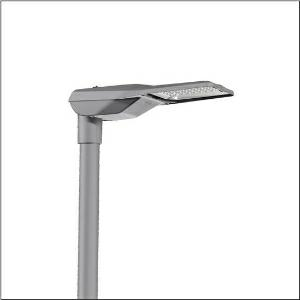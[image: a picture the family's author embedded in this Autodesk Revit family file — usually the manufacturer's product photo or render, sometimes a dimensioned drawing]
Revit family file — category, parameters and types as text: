
# Revit family: streetlight_sl_21_iq_mini___st1_0a_5xe2d31v08jb_ee78
name_source: partatom
category: Lighting Fixtures
units: mm (PartAtom-declared; Revit-internal decimal feet)

## family parameters
Cut with Voids When Loaded = No
Host = Face
Light Source = No
Part Type = Normal
Room Calculation Point = No
Round Connector Dimension = Use Diameter
Shared = No

## types (1)
- --- (1 x LED, 11210 lm, 72.5 W, 3000K)
    Apparent Load = 73 VA
    CIE Flux Codes = 40 73 97 100 100
    Color Rendering = 70
    Color Temperature = 3000K
    Default Elevation = 1800 mm
    Description = Streetlight SL 21 iQ mini, mast luminaire, primary light control with lens, of PMMA, primary optical cover: cover, of toughened safety glass, transparent, light distribution: ST1.0a, light emission: direct distribution, primary light characteristic: asymmetric, installation type: post-top, side-entry, LED, High Power LED, rated luminous flux: 11.210lm, luminous efficacy: 155lm/W, light colour: 730, colour temperature: 3000K, control gear: iQ-Street Remote, D4i with power reduction, control: pre-setting: logarithmic dimming characteristic, Street-Remote, Auto-Match, Temp-Guard, Lumen-Switch, Night-Set, Smart-Wire, Light-Fading, Desk-Remote (wireless, voltage-free reading and setting of iQ features in the workshop via application-optimized NFC function/RFID function), optimised constant luminous flux control (CLO 2.0), mains connection: 220..240V, AC, 50/60Hz, start of lifetime: 73W, end of service life: 76W, reduction: 33W, luminaire housing, of diecast aluminium, powder-coated, Siteco® metallic grey (DB 702S), corrosivity category C5 mid according to DIN EN ISO 12944, please order mast flange separately, inclination adjustable: 0°, 5°, 10°, 15°, sealing non-destructively replaceable, multi-level sealing system, length: 628mm, width: 235mm, height: 110mm, mast flange for spigot size: 42mm (side-entry): 5XC10008XM4, 60/48mm (side-entry/post-top): 5XC10108XM2, 76/60mm (side-entry/post-top): 5XC10108XM1, mounting height: 4..8m, Smart Interface above, protection rating (complete): IP66, insulation class (complete): insulation class II (safety insulation), certification: CE, ENEC, ENEC+, VDE, impact resistance: IK10, permissible operating ambient temperature for outdoor applications: -40..+50°C, standard-compliant lighting for roads and squares, packaging unit: 1 piece

Light Distribution: ST1.0a
    Height = 110 mm
    Lamp = 1 x LED
    Lamp Light Flux = 11210 lm
    Lamp Power = 72.5 W
    Lamp count = 1
    Length = 625 mm
    Luminous efficacy = 155 lm/W
    Manufacturer = Siteco
    ModVariant = No
    Model = 5XE2D31V08JB
    Number of Poles = 1
    OnlyDefault = Yes
    Power Factor = 1
    Product Name = Streetlight SL 21 iQ mini | ST1.0a
    Product group = mast luminaire | pylon top
    ProductGroupID = 6100
    Protection Class = Protection class II
    Protection Degree = IP 66
    RLX_Detail_Level = 1
    RLX_Emergency_Light_Flux = 0 lm
    RLX_Emergency_Type = 0
    RLX_Emergency_Type_DB = No
    RlxData = <blob elided: 92577 chars, md5=b3f45974>
    Socket = socket
    Standby Power = 0 W
    System Light Flux = 11210 lm
    System Power = 73 W
    Type Comments = factory setting: luminous flux: 100 % | dim-lin: 254 | 755 mA
    Type Image = l_1003515.jpg
    URL = http://relux.com
    VarID = @adj_135663
    Voltage = 0 V
    Weight = 0.00 kg
    Width = 234 mm

## geometry (parser evidence)
native form markers: Blend x4, Sweep x10
no freeform markers — native parametric forms only
